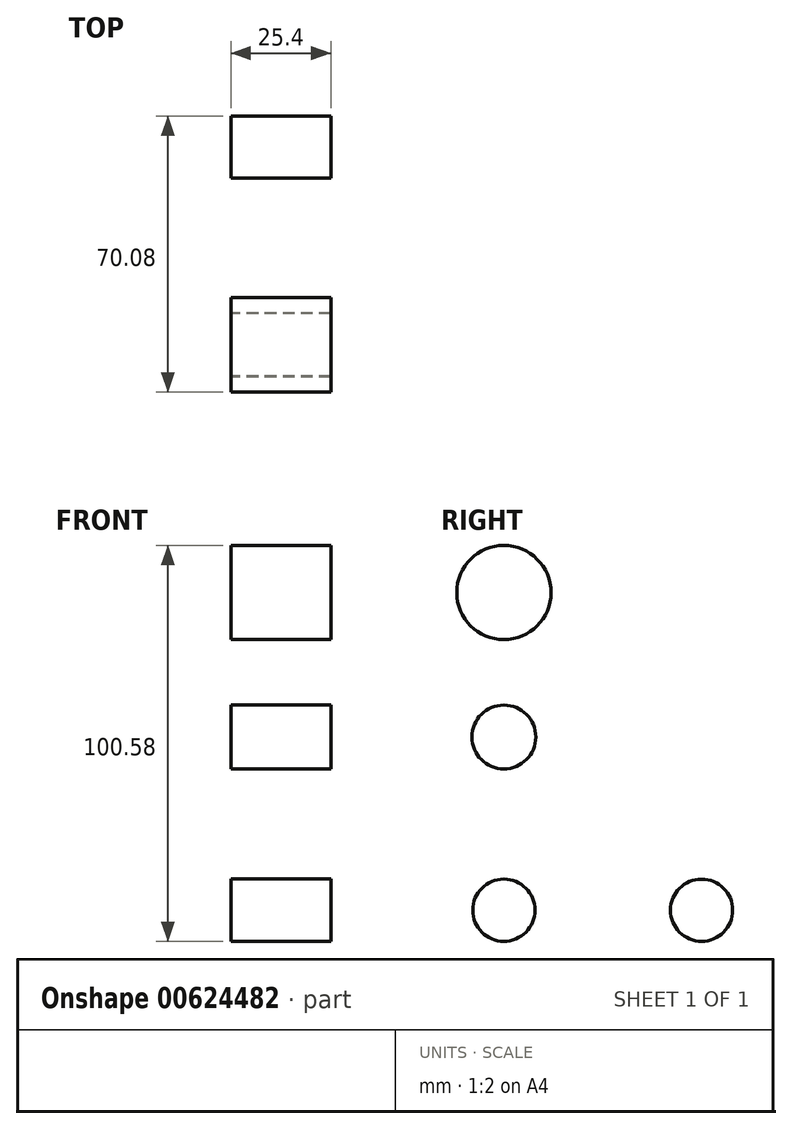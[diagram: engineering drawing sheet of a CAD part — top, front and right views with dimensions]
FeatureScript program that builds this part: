
annotation { "Feature Type Name" : "Feature", "Feature Type Description" : "" }
export const myFeature = defineFeature(function(context is Context, id is Id, definition is map)
    precondition{}
    {
        {
            var Q0;
            Q0=qCreatedBy(makeId("Right.planeOp"),FACE);
            var sketch = newSketch(context, id + "F0", { "sketchPlane" : qUnion([Q0])});
            skLineSegment(sketch, "E0", {"start": v(3.4, 46.04) * mm, "end": v(3.4, -34.67) * mm});
            skLineSegment(sketch, "E1", {"start": v(3.4, -34.67) * mm, "end": v(53.62, -34.67) * mm});
            skCircle(sketch, "E2", {"center": v(3.4, 9.34) * mm, "radius": 8.11 * mm});
            skCircle(sketch, "E3", {"center": v(3.4, -34.67) * mm, "radius": 7.9 * mm});
            skCircle(sketch, "E4", {"center": v(53.62, -34.67) * mm, "radius": 7.9 * mm});
            skCircle(sketch, "E5", {"center": v(3.4, 46.04) * mm, "radius": 11.97 * mm});
            skSolve(sketch);
        }
        {
            var Q0;
            Q0 = qSketchRegion(id + "F0", true);
            extrude(context, id + "F1", {"entities" : qUnion([Q0]), "depth" : 25.4 * mm, "offsetDistance" : 25.4 * mm});
        }
    });
